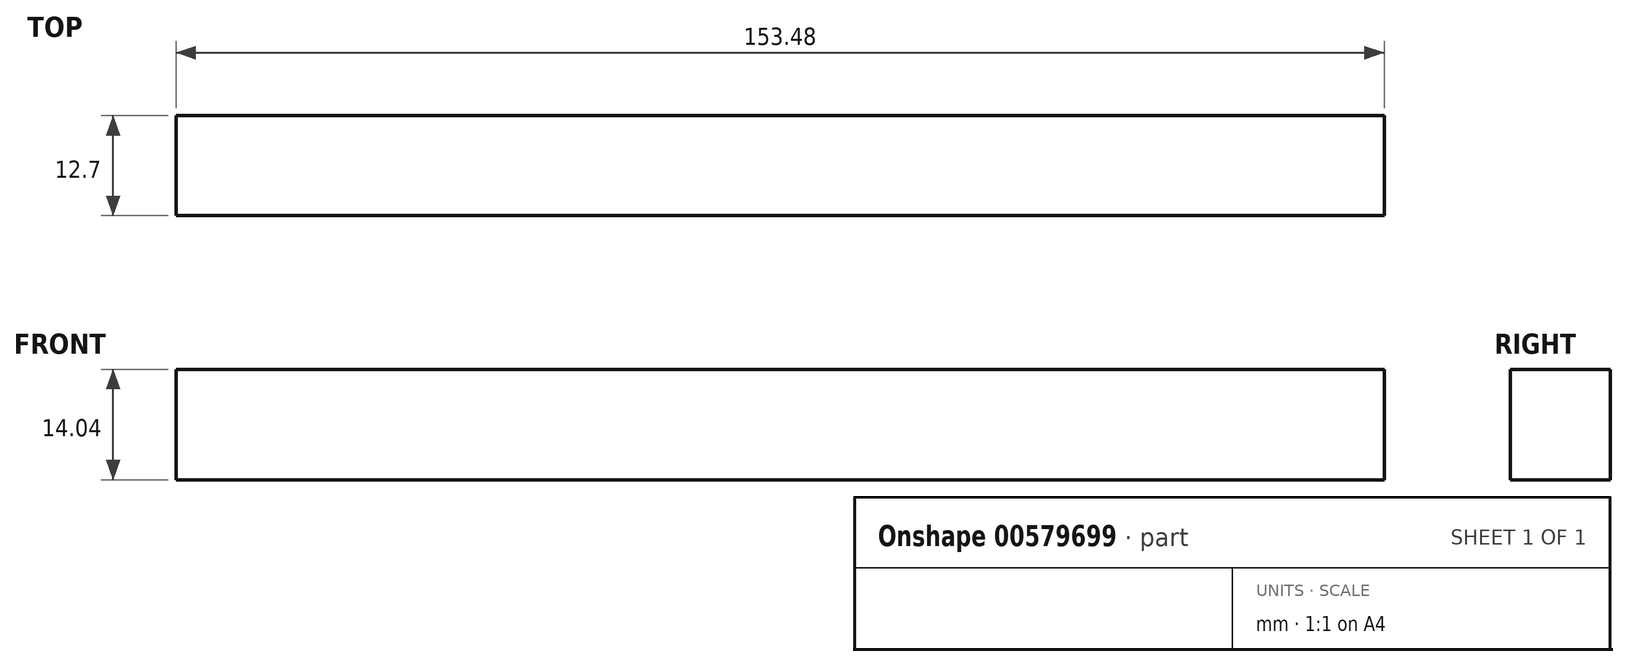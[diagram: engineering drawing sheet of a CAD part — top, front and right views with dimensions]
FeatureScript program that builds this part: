
annotation { "Feature Type Name" : "Feature", "Feature Type Description" : "" }
export const myFeature = defineFeature(function(context is Context, id is Id, definition is map)
    precondition{}
    {
        {
            var Q0;
            Q0=qCreatedBy(makeId("Front.planeOp"),FACE);
            var sketch = newSketch(context, id + "F0", { "sketchPlane" : qUnion([Q0])});
            skLineSegment(sketch, "E0", {"start": v(0, 0) * mm, "end": v(-76.22, 0) * mm});
            skLineSegment(sketch, "E1", {"start": v(-76.22, 0) * mm, "end": v(-76.22, -14.04) * mm});
            skLineSegment(sketch, "E2", {"start": v(-76.22, -14.04) * mm, "end": v(77.26, -14.04) * mm});
            skLineSegment(sketch, "E3", {"start": v(77.26, -14.04) * mm, "end": v(77.26, 0) * mm});
            skLineSegment(sketch, "E4", {"start": v(77.26, 0) * mm, "end": v(0, 0) * mm});
            skSolve(sketch);
        }
        {
            var Q0;
            Q0=makeQuery(id+"F0.imprint","IMPRINT",FACE,{"disambiguationData":[TD([[makeQuery(id+"F0.imprint","IMPRINT",EDGE,{"derivedFrom":sQuery(id+"F0.wireOp",EDGE,"E0")}),1.0]])]});
            extrude(context, id + "F1", {"entities" : qUnion([Q0]), "depth" : 12.7 * mm, "offsetDistance" : 25.4 * mm});
        }
    });
